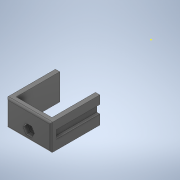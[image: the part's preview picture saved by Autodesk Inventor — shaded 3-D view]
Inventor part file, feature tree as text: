
AUTODESK INVENTOR PART (.ipt)
format: ipt  version: 2020 (Build 240168000, 168)  size: 448,512 bytes
history: native  units: mm
features: extrude x5, projected_geometry x5, sketch x4, fillet x1
ambient origin geometry x8: Origin, YZ Plane, XZ Plane, XY Plane, X Axis, Y Axis, Z Axis, Center Point
bodies: Body1 (feature_tree)
feature tree (15):
  extrude  "Выдавливание7"  Depth=4.0mm
  extrude  "Выдавливание16"  Depth=25.5mm
  sketch  "Эскиз12"
  extrude  "Выдавливание17"  Depth=3.0mm
  extrude  "Выдавливание18"  Depth=3.0mm
  extrude  "Выдавливание19"  Depth=3.0mm
  fillet  "Сопряжение1"  Radius=20.2mm
  sketch  "Эскиз13"
  sketch  "Эскиз1"
  sketch  "Эскиз10"
  projected_geometry  "Спроецированная петля9"
  projected_geometry  "Спроецированная петля10"
  projected_geometry  "Спроецированная петля11"
  projected_geometry  "Спроецированная петля12"
  projected_geometry  "Спроецированная петля13"
